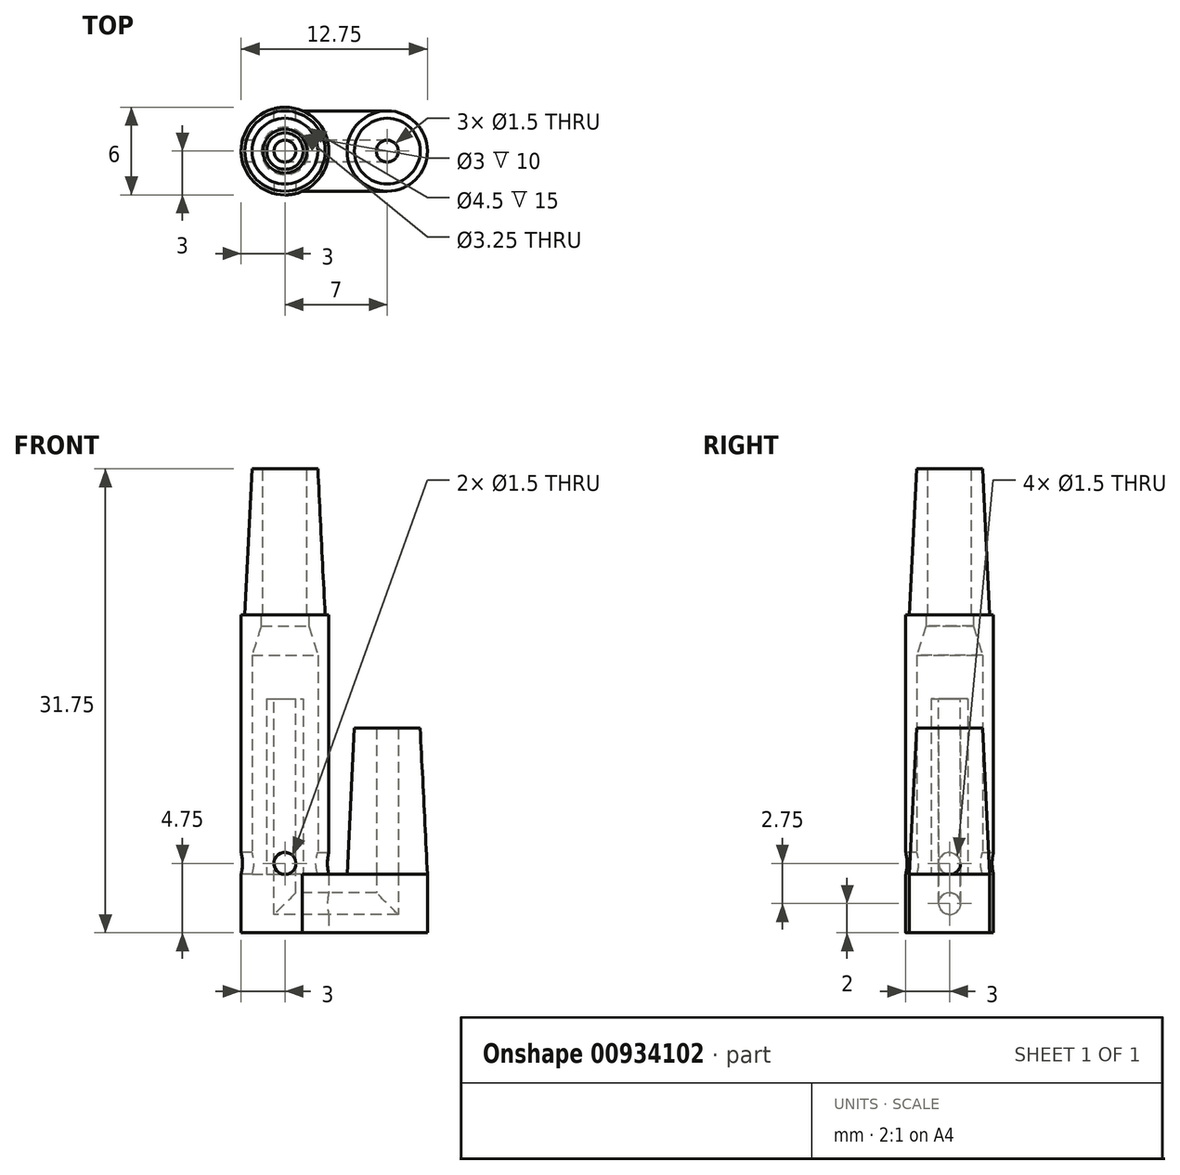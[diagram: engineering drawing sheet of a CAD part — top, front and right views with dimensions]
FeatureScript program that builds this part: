
annotation { "Feature Type Name" : "Feature", "Feature Type Description" : "" }
export const myFeature = defineFeature(function(context is Context, id is Id, definition is map)
    precondition{}
    {
        {
            var Q0;
            Q0=qCreatedBy(makeId("Front.planeOp"),FACE);
            var sketch = newSketch(context, id + "F0", { "sketchPlane" : qUnion([Q0])});
            skLineSegment(sketch, "E0", {"start": v(-2.75, 0) * mm, "end": v(-3, 0) * mm});
            skLineSegment(sketch, "E1", {"start": v(-3, 0) * mm, "end": v(-3, -21.75) * mm});
            skLineSegment(sketch, "E2", {"start": v(-3, -21.75) * mm, "end": v(0, -21.75) * mm});
            skLineSegment(sketch, "E3", {"start": v(0, -21.75) * mm, "end": v(0, -5.75) * mm});
            skLineSegment(sketch, "E4", {"start": v(0, -5.75) * mm, "end": v(-1.25, -5.75) * mm});
            skLineSegment(sketch, "E5", {"start": v(-1.25, -5.75) * mm, "end": v(-1.25, -17.75) * mm});
            skLineSegment(sketch, "E6", {"start": v(-1.25, -17.75) * mm, "end": v(-2.25, -17.75) * mm});
            skLineSegment(sketch, "E7", {"start": v(-2.25, -17.75) * mm, "end": v(-2.25, -2.75) * mm});
            skLineSegment(sketch, "E8", {"start": v(-1.63, -0.75) * mm, "end": v(-1.63, 0) * mm});
            skLineSegment(sketch, "E9", {"start": v(-1.62, -0.75) * mm, "end": v(-2.25, -2.75) * mm});
            skLineSegment(sketch, "E10", {"start": v(0, -21.75) * mm, "end": v(0, -17.75) * mm});
            skLineSegment(sketch, "E11", {"start": v(-2.75, 0) * mm, "end": v(-1.63, 0) * mm});
            skSolve(sketch);
        }
        {
            var Q0;
            Q0=makeQuery(id+"F0.imprint","IMPRINT",FACE,{"disambiguationData":[TD([[makeQuery(id+"F0.imprint","IMPRINT",EDGE,{"derivedFrom":sQuery(id+"F0.wireOp",EDGE,"E1")}),1.0]])]});
            var Q1;
            Q1=sQuery(id+"F0.wireOp",EDGE,"E3");
            revolve(context, id + "F1", {"surfaceOperationType" : NewSurfaceOperationType.NEW, "entities" : qUnion([Q0]), "axis" : qUnion([Q1]), "revolveType" : RevolveType.FULL});
        }
        {
            var Q0;
            Q0=qCreatedBy(makeId("Front.planeOp"),FACE);
            var sketch = newSketch(context, id + "F2", { "sketchPlane" : qUnion([Q0])});
            skLineSegment(sketch, "E12", {"start": v(0, 0) * mm, "end": v(-2.75, 0) * mm});
            skLineSegment(sketch, "E13", {"start": v(-2.75, 0) * mm, "end": v(-2.25, 10) * mm});
            skLineSegment(sketch, "E14", {"start": v(-2.25, 10) * mm, "end": v(0, 10) * mm});
            skLineSegment(sketch, "E15", {"start": v(0, 10) * mm, "end": v(0, 0) * mm});
            skSolve(sketch);
        }
        {
            var Q0;
            Q0=makeQuery(id+"F2.imprint","IMPRINT",FACE,{"disambiguationData":[TD([[makeQuery(id+"F2.imprint","IMPRINT",EDGE,{"derivedFrom":sQuery(id+"F2.wireOp",EDGE,"E12")}),-1.0]])]});
            var Q1;
            Q1=sQuery(id+"F2.wireOp",EDGE,"E15");
            revolve(context, id + "F3", {"surfaceOperationType" : NewSurfaceOperationType.NEW, "entities" : qUnion([Q0]), "axis" : qUnion([Q1]), "revolveType" : RevolveType.FULL});
        }
        {
            var Q0;
            Q0=makeQuery(id+"F3.opRevolve","SWEPT_FACE",FACE,{"disambiguationData":[OSD([sQuery(id+"F2.wireOp",EDGE,"E14")])]});
            var sketch = newSketch(context, id + "F4", { "sketchPlane" : qUnion([Q0])});
            skPoint(sketch, "E16", {"position": v(0, 0) * mm});
            skSolve(sketch);
        }
        {
            var Q0;
            Q0=qCreatedBy(makeId("Front.planeOp"),FACE);
            var sketch = newSketch(context, id + "F5", { "sketchPlane" : qUnion([Q0])});
            skLineSegment(sketch, "E17", {"start": v(0, -19.75) * mm, "end": v(7, -19.75) * mm});
            skLineSegment(sketch, "E18", {"start": v(7, -19.75) * mm, "end": v(7, -17.75) * mm});
            skLineSegment(sketch, "E19", {"start": v(7, -17.75) * mm, "end": v(7, -7.75) * mm});
            skLineSegment(sketch, "E20", {"start": v(0, -19.75) * mm, "end": v(0, 0) * mm});
            skSolve(sketch);
        }
        {
            var Q0;
            Q0=makeQuery(id+"F1.opRevolve","SWEPT_FACE",FACE,{"disambiguationData":[OSD([sQuery(id+"F0.wireOp",EDGE,"E2")])]});
            var sketch = newSketch(context, id + "F6", { "sketchPlane" : qUnion([Q0])});
            skArc(sketch, "E21", {"start": v(0, 2.75) * mm, "mid": v(-2.75, 0) * mm, "end": v(0, -2.75) * mm});
            skLineSegment(sketch, "E22.bottom", {"start": v(0, -2.75) * mm, "end": v(7, -2.75) * mm});
            skLineSegment(sketch, "E22.top", {"start": v(0, 2.75) * mm, "end": v(7, 2.75) * mm});
            skArc(sketch, "E23", {"start": v(7, -2.75) * mm, "mid": v(9.75, 0) * mm, "end": v(7, 2.75) * mm});
            skSolve(sketch);
        }
        {
            var Q0;
            {var subQ0=sQuery(id+"F6.wireOp",EDGE,"E23");Q0=makeQuery(id+"F6.imprint","IMPRINT",FACE,{"disambiguationData":[TD([[makeQuery(id+"F6.imprint","IMPRINT",EDGE,{"derivedFrom":subQ0}),1.0]])]});}
            extrude(context, id + "F7", {"entities" : qUnion([Q0]), "oppositeDirection" : true, "depth" : 4 * mm, "offsetDistance" : 25 * mm});
        }
        {
            var Q0;
            Q0=makeQuery(id+"F3.opRevolve","SWEPT_BODY",BODY,{"disambiguationData":[OSD([sQuery(id+"F2.wireOp",EDGE,"E12"),sQuery(id+"F2.wireOp",EDGE,"E13"),sQuery(id+"F2.wireOp",EDGE,"E14"),sQuery(id+"F2.wireOp",EDGE,"E15")])]});
            var Q1;
            Q1=sQuery(id+"F5.wireOp",VERTEX,"E20.end");
            var Q2;
            Q2=sQuery(id+"F5.wireOp",VERTEX,"E18.end");
            transform(context, id + "F8", {"entities" : qUnion([Q0]), "transformType" : TransformType.TRANSLATION_ENTITY, "oppositeDirectionEntity" : false, "transformLine" : qUnion([Q1, Q2]), "makeCopy" : true});
        }
        {
            var Q0;
            Q0=sQuery(id+"F4.wireOp",VERTEX,"E16");
            var Q1;
            Q1=makeQuery(id+"F3.opRevolve","SWEPT_BODY",BODY,{"disambiguationData":[OSD([sQuery(id+"F2.wireOp",EDGE,"E12"),sQuery(id+"F2.wireOp",EDGE,"E13"),sQuery(id+"F2.wireOp",EDGE,"E14"),sQuery(id+"F2.wireOp",EDGE,"E15")])]});
            hole(context, id + "F9", {"style" : HoleStyle.SIMPLE, "endStyle" : HoleEndStyle.THROUGH, "holeDiameter" : 3 * mm, "majorDiameter" : 5 * mm, "isTappedThrough" : true, "tappedDepth" : 12 * mm, "tapClearance" : 3, "locations" : qUnion([Q0]), "scope" : qUnion([Q1])});
        }
        {
            var Q0;
            Q0=makeQuery(id+"F8.opPattern","COPY",FACE,{"derivedFrom":makeQuery(id+"F3.opRevolve","SWEPT_FACE",FACE,{"disambiguationData":[OSD([sQuery(id+"F2.wireOp",EDGE,"E14")])]}),"instanceName":"1"});
            var sketch = newSketch(context, id + "F10", { "sketchPlane" : qUnion([Q0])});
            skCircle(sketch, "E24", {"center": v(7, 0) * mm, "radius": 0.75 * mm});
            skSolve(sketch);
        }
        {
            var Q0;
            Q0=makeQuery(id+"F10.imprint","IMPRINT",FACE,{"disambiguationData":[TD([[makeQuery(id+"F10.imprint","IMPRINT",EDGE,{"derivedFrom":sQuery(id+"F10.wireOp",EDGE,"E24")}),1.0]])]});
            var Q1;
            Q1 = qConstructionFilter(qBodyType(qCreatedBy(id + "F5" ,EDGE), BodyType.WIRE), ConstructionObject.NO);
            sweep(context, id + "F11", {"operationType" : NewBodyOperationType.REMOVE, "profiles" : qUnion([Q0]), "path" : qUnion([Q1])});
        }
        {
            var Q0;
            Q0=makeQuery(id+"F7.opExtrude","CAP_FACE",FACE,{"disambiguationData":[OSD([sQuery(id+"F0.wireOp",EDGE,"E1"),sQuery(id+"F0.wireOp",EDGE,"E2"),sQuery(id+"F6.wireOp",EDGE,"E22.bottom"),sQuery(id+"F6.wireOp",EDGE,"E22.top"),sQuery(id+"F6.wireOp",EDGE,"E23")])],"isStart":false});
            var sketch = newSketch(context, id + "F12", { "sketchPlane" : qUnion([Q0])});
            skLineSegment(sketch, "E25", {"start": v(1.5, 0) * mm, "end": v(3, 0) * mm});
            skLineSegment(sketch, "E26", {"start": v(3, 0) * mm, "end": v(1.5, 0) * mm});
            skPoint(sketch, "E27.orphan", {"position": v(0, 0) * mm});
            skSolve(sketch);
        }
        {
            var Q0;
            Q0=qCreatedBy(makeId("Right.planeOp"),FACE);
            cPlane(context, id + "F13", {"entities" : qUnion([Q0]), "cplaneType" : CPlaneType.OFFSET, "offset" : 2.75 * mm, "width" : 150 * mm, "height" : 150 * mm});
        }
        {
            var Q0;
            Q0=qCreatedBy(id+"F13.planeOp",FACE);
            var sketch = newSketch(context, id + "F14", { "sketchPlane" : qUnion([Q0])});
            skCircle(sketch, "E28", {"center": v(0, -17) * mm, "radius": 0.75 * mm});
            skSolve(sketch);
        }
        {
            var Q0;
            Q0 = qSketchRegion(id + "F14", true);
            var Q1;
            Q1=sQuery(id+"F12.wireOp",EDGE,"E25");
            sweep(context, id + "F15", {"profiles" : qUnion([Q0]), "path" : qUnion([Q1])});
        }
        {
            var Q0;
            Q0=makeQuery(id+"F15.opSweep","SWEPT_BODY",BODY,{"disambiguationData":[OSD([sQuery(id+"F12.wireOp",EDGE,"E25"),sQuery(id+"F14.wireOp",EDGE,"E28")])]});
            var Q1;
            Q1=sQuery(id+"F0.wireOp",EDGE,"E3");
            circularPattern(context, id + "F16", {"entities" : qUnion([Q0]), "axis" : qUnion([Q1]), "angle" : 360 * degree, "instanceCount" : 4, "equalSpace" : true});
        }
        {
            var Q0;
            Q0=makeQuery(id+"F15.opSweep","SWEPT_BODY",BODY,{"disambiguationData":[OSD([sQuery(id+"F12.wireOp",EDGE,"E25"),sQuery(id+"F14.wireOp",EDGE,"E28")])]});
            var Q1;
            Q1=makeQuery(id+"F16.opPattern","COPY",BODY,{"derivedFrom":makeQuery(id+"F15.opSweep","SWEPT_BODY",BODY,{"disambiguationData":[OSD([sQuery(id+"F12.wireOp",EDGE,"E25"),sQuery(id+"F14.wireOp",EDGE,"E28")])]}),"instanceName":"3"});
            var Q2;
            Q2=makeQuery(id+"F16.opPattern","COPY",BODY,{"derivedFrom":makeQuery(id+"F15.opSweep","SWEPT_BODY",BODY,{"disambiguationData":[OSD([sQuery(id+"F12.wireOp",EDGE,"E25"),sQuery(id+"F14.wireOp",EDGE,"E28")])]}),"instanceName":"2"});
            var Q3;
            Q3=makeQuery(id+"F16.opPattern","COPY",BODY,{"derivedFrom":makeQuery(id+"F15.opSweep","SWEPT_BODY",BODY,{"disambiguationData":[OSD([sQuery(id+"F12.wireOp",EDGE,"E25"),sQuery(id+"F14.wireOp",EDGE,"E28")])]}),"instanceName":"1"});
            var Q4;
            Q4=makeQuery(id+"F1.opRevolve","SWEPT_BODY",BODY,{"disambiguationData":[OSD([sQuery(id+"F0.wireOp",EDGE,"E0"),sQuery(id+"F0.wireOp",EDGE,"E1"),sQuery(id+"F0.wireOp",EDGE,"E2"),sQuery(id+"F0.wireOp",EDGE,"E3"),sQuery(id+"F0.wireOp",EDGE,"E4"),sQuery(id+"F0.wireOp",EDGE,"E5"),sQuery(id+"F0.wireOp",EDGE,"E6"),sQuery(id+"F0.wireOp",EDGE,"E7"),sQuery(id+"F0.wireOp",EDGE,"E8"),sQuery(id+"F0.wireOp",EDGE,"E9"),sQuery(id+"F0.wireOp",EDGE,"E10"),sQuery(id+"F0.wireOp",EDGE,"E11")])]});
            booleanBodies(context, id + "F17", {"operationType" : BooleanOperationType.SUBTRACTION, "tools" : qUnion([Q0, Q1, Q2, Q3]), "targets" : qUnion([Q4])});
        }
    });
